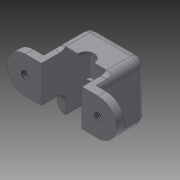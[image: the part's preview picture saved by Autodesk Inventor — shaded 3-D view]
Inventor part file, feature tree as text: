
AUTODESK INVENTOR PART (.ipt)
format: ipt  version: 2013 (Build 170138000, 138)  size: 220,672 bytes
history: native  units: mm
features: sketch x7, extrude x6, fillet x3, hole x1, mirror x1
ambient origin geometry x8: Origin, YZ Plane, XZ Plane, XY Plane, X Axis, Y Axis, Z Axis, Center Point
bodies: Solid1 (feature_tree)
feature tree (18):
  extrude  "Extrusion1"  Depth=12.0mm
  extrude  "Extrusion2"  Depth=2.0mm
  extrude  "Extrusion3"  Depth=0.6mm TaperAngle=0.0deg
  extrude  "Extrusion4"  Depth=5.0mm
  extrude  "Extrusion5"  Depth=5.0mm TaperAngle=0.0deg
  extrude  "Extrusion6"  Depth=5.0mm TaperAngle=0.0deg
  fillet  "Fillet1"  Radius=2.0mm
  hole  "Hole2"  [1 undecoded]
  mirror  "Mirror1"
  fillet  "Fillet2"  Radius=2.0mm
  fillet  "Fillet3"  Radius=2.0mm
  sketch  "Sketch1"  dims[d0=10.0mm d2=12.0mm]
  sketch  "Sketch2"  dims[d3=2.0mm d4=2.0mm]
  sketch  "Sketch3"  dims[d5=9.0mm d6=0.0mm d7=0.6mm d8=0.0mm]
  sketch  "Sketch4"  dims[d9=5.0mm d10=0.0mm d11=5.0mm]
  sketch  "Sketch5"  dims[d14=12.0mm d15=5.0mm d16=0.0mm]
  sketch  "Sketch6"  dims[d17=4.0mm d18=5.0mm d19=0.0mm d20=2.0mm]
  sketch  "Sketch8"  dims[d22=6.5mm d23=0.0mm d32=4.5mm d33=2.013mm d34=6.0mm d35=4.0mm d36=2.0mm d37=90.0deg d38=8.0mm d39=20.594885mm d40=2.0mm d41=2.0mm]
note: 1 required parameter value undecoded (feature->parameter linkage not recoverable at this tier; creation-order binding heuristic only, values carry confidence <= 0.55)
